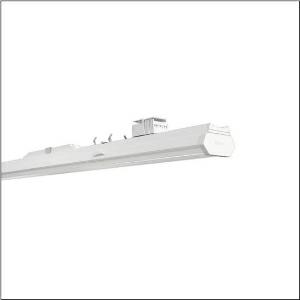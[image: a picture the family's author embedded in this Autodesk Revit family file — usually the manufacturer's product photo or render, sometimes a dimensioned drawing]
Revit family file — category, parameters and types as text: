
# Revit family: licross_r__21_protected_mo_52tp12dn4axg_691a
name_source: partatom
category: Lighting Fixtures
units: mm (PartAtom-declared; Revit-internal decimal feet)

## family parameters
Cut with Voids When Loaded = No
Host = Face
Light Source = No
Part Type = Normal
Room Calculation Point = No
Round Connector Dimension = Use Diameter
Shared = No

## types (1)
- --- (1 x LED, 10000 lm, 57.5 W, 4000K)
    Apparent Load = 58 VA
    CIE Flux Codes = 73 92 98 99 100
    Color Rendering = 80
    Color Temperature = 4000K
    Default Elevation = 1800 mm
    Description = Licross® 21 Protected MO, luminaire insert, of sheet steel, galvanised, coil coated, white, length: 1.500mm, width: 90mm, height: 103mm, LED rated luminous flux: 10.000lm, light colour: 840, control gear: DALI 2, with plug, 5-pole, with phase selection, mains connection: 220..240V, AC, 50/60Hz, rated input power: 58W, halogen-free wiring, primary light control with lens, of plastic, primary optical cover: cover, of PMMA, light emission: direct distribution, primary light characteristic: symmetric, protection rating (complete): IP64, insulation class (complete): insulation class I (protective earthing), certification: CE, ENEC, VDE, UKCA, protection symbol: D if used in an environment with conductive dust loads with corresponding accessories, impact resistance: IK06, permissible ambient temperature for indoor applications: -25..+40°C, corresponds to IFS (International Featured Standards) requirements for safety and quality in the food industry, reducing of maximum allowable ambient temperature of 5°C with ceiling mounting, LABS conformity tested according to VDMA 24364:2018-05, packaging unit: 1 piece
    Height = 92 mm
    Lamp = 1 x LED
    Lamp Light Flux = 10000 lm
    Lamp Power = 57.5 W
    Lamp count = 1
    Length = 1500 mm
    Luminous efficacy = 174 lm/W
    Manufacturer = Siteco
    ModVariant = No
    Model = 52TP12DN4AXG
    Mounting Place = Ceiling
    Mounting Type = Pendant
    Number of Poles = 1
    OnlyDefault = Yes
    Power Factor = 1
    Product Name = Licross® 21 Protected MO
    Product group = luminaire insert
    ProductGroupID = 902
    Protection Class = Protection class I
    Protection Degree = IP 64
    RLX_Detail_Level = 1
    RLX_Emergency_Light_Flux = 0 lm
    RLX_Emergency_Type = 0
    RLX_Emergency_Type_DB = No
    RlxData = <blob elided: 24301 chars, md5=665f22cf>
    Socket = socket
    Standby Power = 0 W
    System Light Flux = 10000 lm
    System Power = 58 W
    Type Comments = factory setting: luminous flux: 100 % | dim-lin: 254 | 388 mA
    Type Image = l_1256148.jpg
    URL = http://relux.com
    VarID = @adj_128594
    Voltage = 0 V
    Weight = 0.00 kg
    Width = 88 mm

## geometry (parser evidence)
native form markers: Blend x4, Sweep x11
no freeform markers — native parametric forms only
